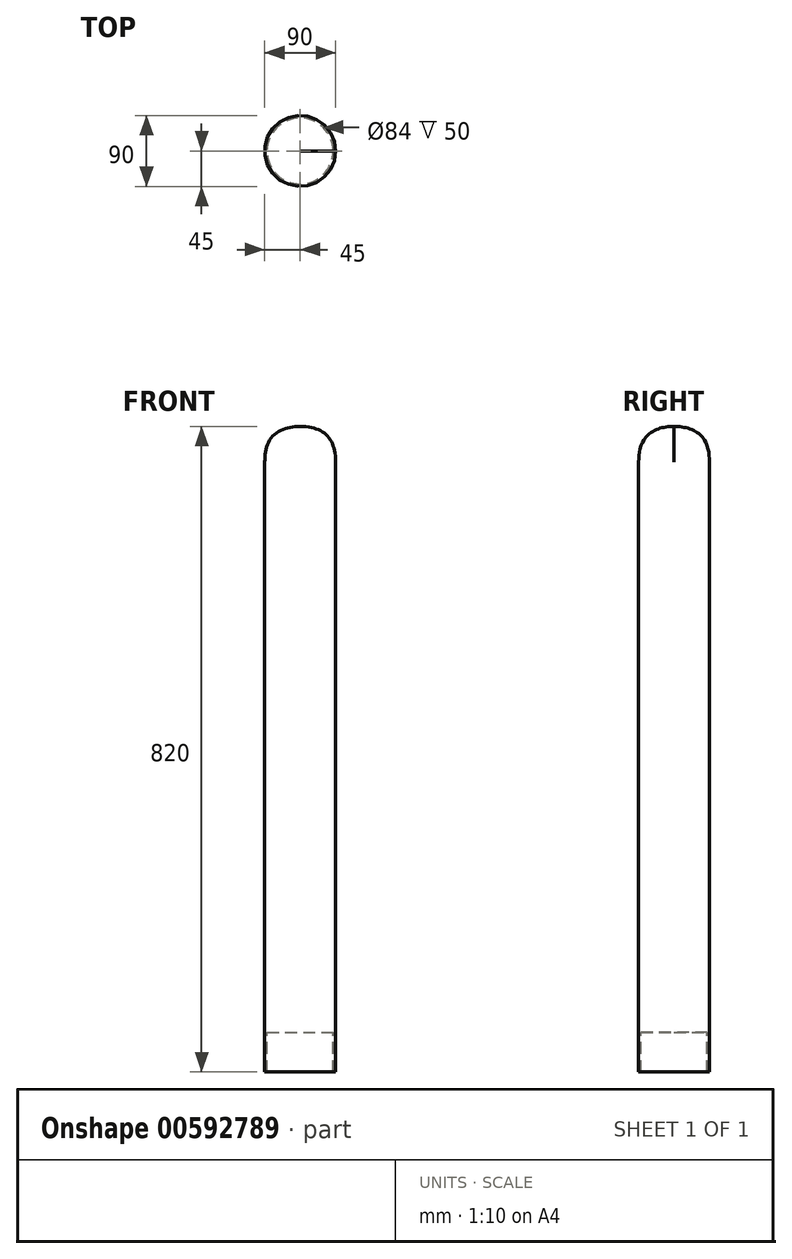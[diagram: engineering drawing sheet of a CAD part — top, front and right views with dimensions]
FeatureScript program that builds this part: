
annotation { "Feature Type Name" : "Feature", "Feature Type Description" : "" }
export const myFeature = defineFeature(function(context is Context, id is Id, definition is map)
    precondition{}
    {
        {
            var Q0;
            Q0=qCreatedBy(makeId("Top.planeOp"),FACE);
            var sketch = newSketch(context, id + "F0", { "sketchPlane" : qUnion([Q0])});
            skCircle(sketch, "E0", {"center": v(0, 0) * mm, "radius": 45 * mm});
            skSolve(sketch);
        }
        {
            var Q0;
            Q0 = qSketchRegion(id + "F0", true);
            extrude(context, id + "F1", {"entities" : qUnion([Q0]), "endBound" : BoundingType.SYMMETRIC, "depth" : (820 - 50) * mm, "offsetDistance" : 25 * mm});
        }
        {
            var Q0;
            Q0=makeQuery(id+"F1.opExtrude","CAP_FACE",FACE,{"disambiguationData":[OSD([sQuery(id+"F0.wireOp",EDGE,"E0")])],"isStart":false});
            fillet(context, id + "F2", {"entities" : qUnion([Q0]), "radius" : 45 * mm, "tangentPropagation" : true, "rho" : 0.5, "crossSection" : FilletCrossSection.CONIC, "allowEdgeOverflow" : false});
        }
        {
            var Q0;
            Q0=makeQuery(id+"F1.opExtrude","CAP_FACE",FACE,{"disambiguationData":[OSD([sQuery(id+"F0.wireOp",EDGE,"E0")])],"isStart":true});
            var sketch = newSketch(context, id + "F3", { "sketchPlane" : qUnion([Q0])});
            skCircle(sketch, "E1", {"center": v(0, 0) * mm, "radius": 42 * mm});
            skCircle(sketch, "E2", {"center": v(0, 0) * mm, "radius": 45 * mm});
            skSolve(sketch);
        }
        {
            var Q0;
            Q0 = qSketchRegion(id + "F3", true);
            extrude(context, id + "F4", {"entities" : qUnion([Q0]), "operationType" : NewBodyOperationType.ADD, "depth" : 50 * mm, "offsetDistance" : 25 * mm});
        }
    });
